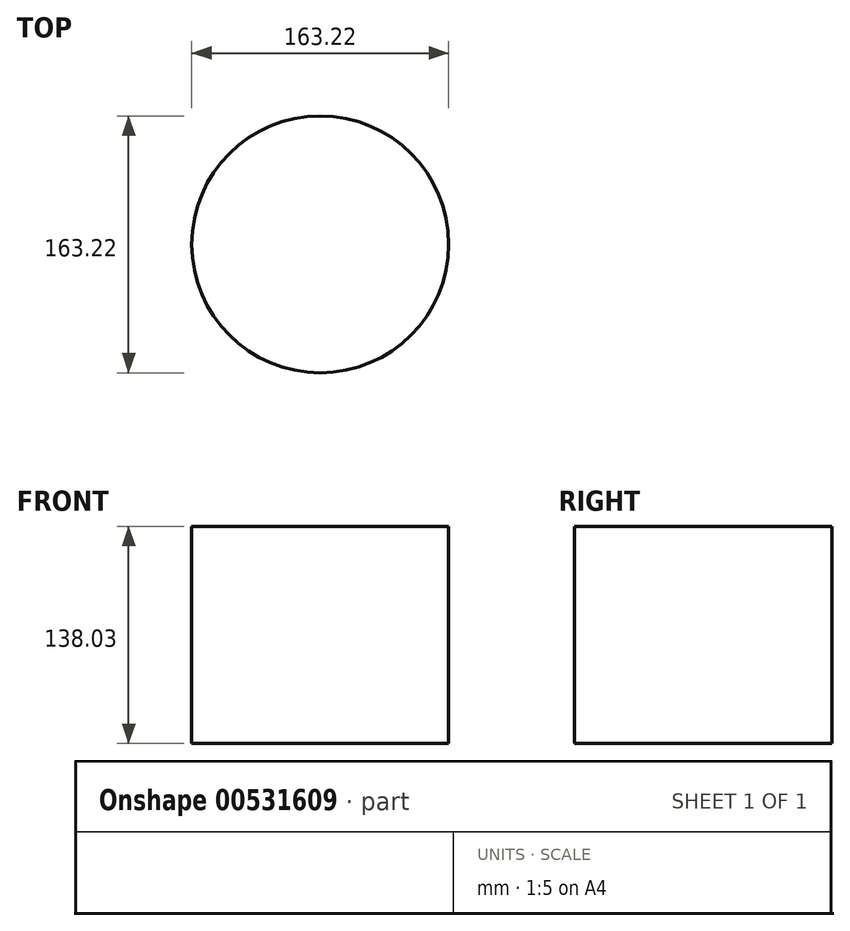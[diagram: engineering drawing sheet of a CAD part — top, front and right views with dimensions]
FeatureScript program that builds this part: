
annotation { "Feature Type Name" : "Feature", "Feature Type Description" : "" }
export const myFeature = defineFeature(function(context is Context, id is Id, definition is map)
    precondition{}
    {
        {
            var Q0;
            Q0=qCreatedBy(makeId("Top.planeOp"),FACE);
            var sketch = newSketch(context, id + "F0", { "sketchPlane" : qUnion([Q0])});
            skCircle(sketch, "E0", {"center": v(0, 0) * mm, "radius": 81.6 * mm});
            skSolve(sketch);
        }
        {
            var Q0;
            Q0=makeQuery(id+"F0.imprint","IMPRINT",FACE,{"disambiguationData":[TD([[makeQuery(id+"F0.imprint","IMPRINT",EDGE,{"derivedFrom":sQuery(id+"F0.wireOp",EDGE,"E0")}),1.0]])]});
            extrude(context, id + "F1", {"entities" : qUnion([Q0]), "depth" : 113.03 * mm, "offsetDistance" : 25.4 * mm});
        }
        {
            var Q0;
            Q0=makeQuery(id+"F1.opExtrude","CAP_FACE",FACE,{"disambiguationData":[OSD([sQuery(id+"F0.wireOp",EDGE,"E0")])],"isStart":false});
            extrude(context, id + "F2", {"entities" : qUnion([Q0]), "operationType" : NewBodyOperationType.ADD, "depth" : 25 * mm, "offsetDistance" : 25 * mm});
        }
    });
